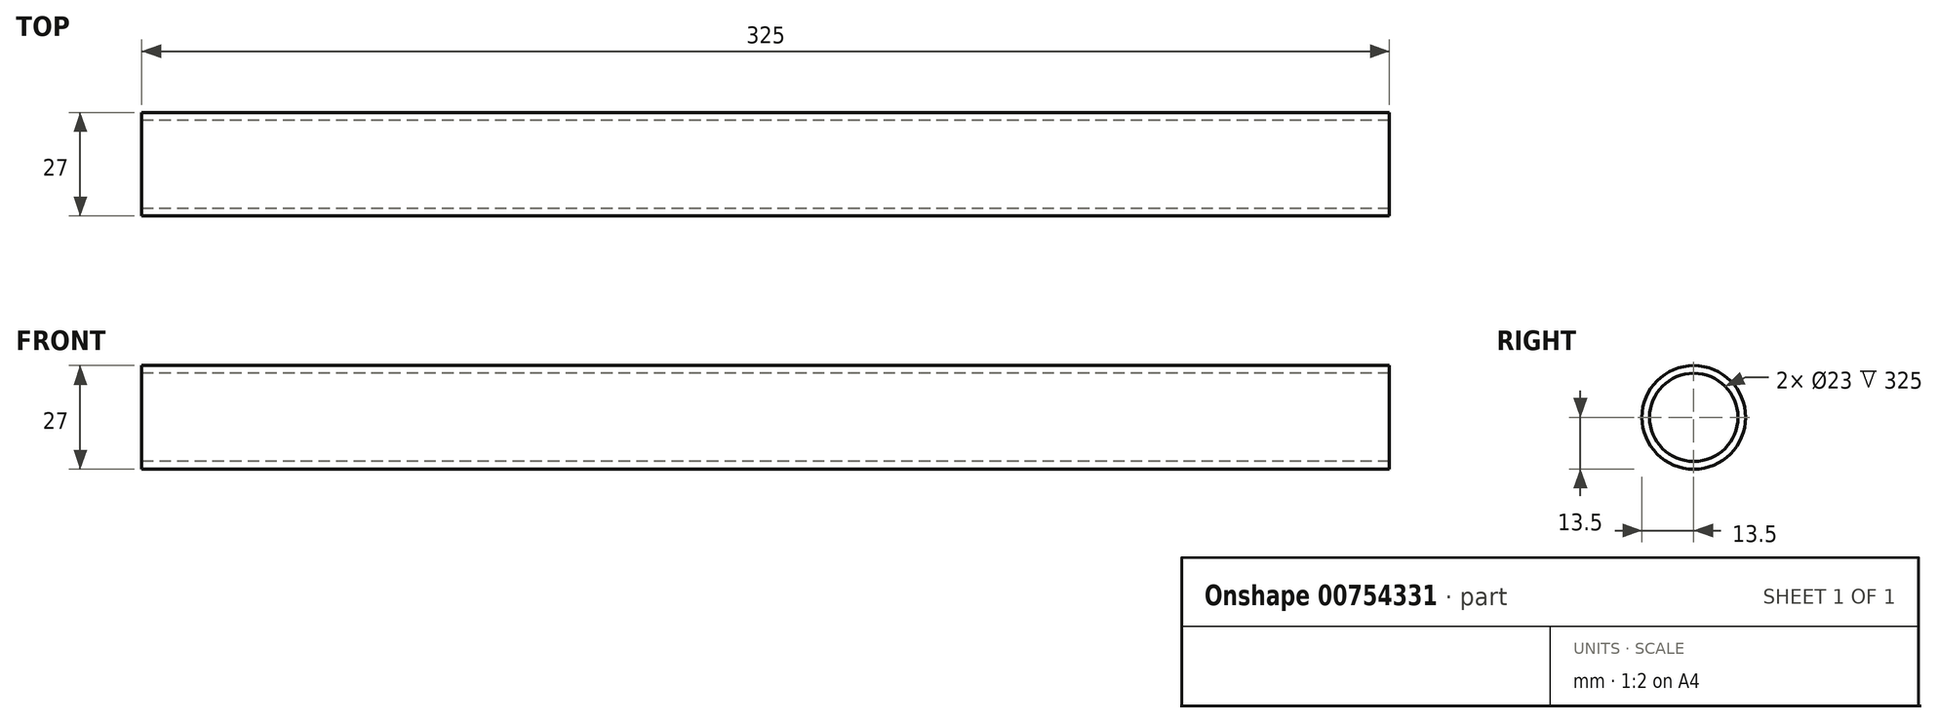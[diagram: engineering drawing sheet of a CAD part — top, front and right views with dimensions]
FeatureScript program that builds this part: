
annotation { "Feature Type Name" : "Feature", "Feature Type Description" : "" }
export const myFeature = defineFeature(function(context is Context, id is Id, definition is map)
    precondition{}
    {
        {
            var Q0;
            Q0=qCreatedBy(makeId("Right.planeOp"),FACE);
            var sketch = newSketch(context, id + "F0", { "sketchPlane" : qUnion([Q0])});
            skCircle(sketch, "E0", {"center": v(0, 0) * mm, "radius": 13.5 * mm});
            skCircle(sketch, "E1", {"center": v(0, 0) * mm, "radius": 11.5 * mm});
            skSolve(sketch);
        }
        {
            var Q0;
            Q0 = qSketchRegion(id + "F0", true);
            extrude(context, id + "F1", {"entities" : qUnion([Q0]), "depth" : 325 * mm, "offsetDistance" : 25 * mm});
        }
    });
